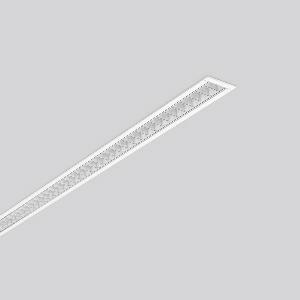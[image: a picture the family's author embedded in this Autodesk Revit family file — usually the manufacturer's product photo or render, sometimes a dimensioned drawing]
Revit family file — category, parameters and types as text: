
# Revit family: less_is_more_27_312177_002_1_76_c780
name_source: partatom
category: Lighting Fixtures
units: mm (PartAtom-declared; Revit-internal decimal feet)

## family parameters
Cut with Voids When Loaded = No
Host = Face
Light Source = No
Part Type = Normal
Room Calculation Point = No
Round Connector Dimension = Use Diameter
Shared = No

## types (1)
- LESS IS MORE 27 (1 x LED Modul 840, 2350 lm, 4000)
    Apparent Load = 25 VA
    CIE Flux Codes = 90 99 100 100 100
    Color Rendering = 80
    Color Temperature = 4000
    Default Elevation = 1800 mm
    Description = Series: LESS IS MORE 27
Recessed ceiling and wall luminaire with slim design. Housing: extruded aluminium profile, powder-coated. End cap aluminium powder-coated. High polish aluminium micro grid. Perfect for office areas (RUG < 19) and environments with computer screens in accordance with EN 12464-1. Suitable for Recessed ceiling mounting, wall (recessed). External driver with connecting cable. 
Colour: traffic white, matt (RAL 9016)
Length: 1014 mm
Width: 38 mm
Height: 2 mm
Cut-out length: 1006 mm
Cut-out width: 30 mm
Recess height: 45-60 mm
Luminaire: recess height: 37 mm
Lamp: LED
Socket: without socket
Colour temperature: 4000K
Colour rendering index (CRI): 82
System power: 25 W
Rated luminous flux: 2350 lm
Luminous efficiency: 94 lm/W
Control gear: Voltage converter, DALI dim.
Protection class: II
Type of protection: IP 20
    Height = 0 mm  [stored 0 ft]
    Lamp = 1 x LED Modul 840
    Lamp Light Flux = 2350 lm
    Lamp count = 1
    Length = 1014 mm
    Lifetime = 50000 h
    Luminous efficacy = 94 lm/W
    Manufacturer = RZB
    ModVariant = No
    Model = 312177.002.1.76
    Mounting Place = Ceiling, Wall
    Mounting Type = Recessed
    Number of Poles = 1
    OnlyDefault = Yes
    Power Factor = 1
    Product Name = LESS IS MORE 27
    Product group = Recessed LED linear luminaires
    ProductGroupID = 407
    Protection Class = Protection class II
    Protection Degree = IP 20
    RLX_Detail_Level = 1
    RLX_Emergency_Light_Flux = 0 lm
    RLX_Emergency_Type = 0
    RLX_Emergency_Type_DB = No
    RlxData = <blob elided: 27025 chars, md5=d24614e1>
    Socket = socket
    Standby Power = 0 W
    System Light Flux = 2350 lm
    System Power = 25 W
    Type Comments = Product without accessories
    Type Image = 312177.002.jpg
    URL = http://relux.com
    VarID = ---
    Voltage = 230 V
    Voltage Range = 220-240 V
    Weight = 0.00 kg
    Width = 38 mm

note: [stored X ft] marks values corroborated as IEEE doubles in the binary element streams (Revit-internal decimal feet)

## geometry (parser evidence)
native form markers: Blend x4, Sweep x14
no freeform markers — native parametric forms only
